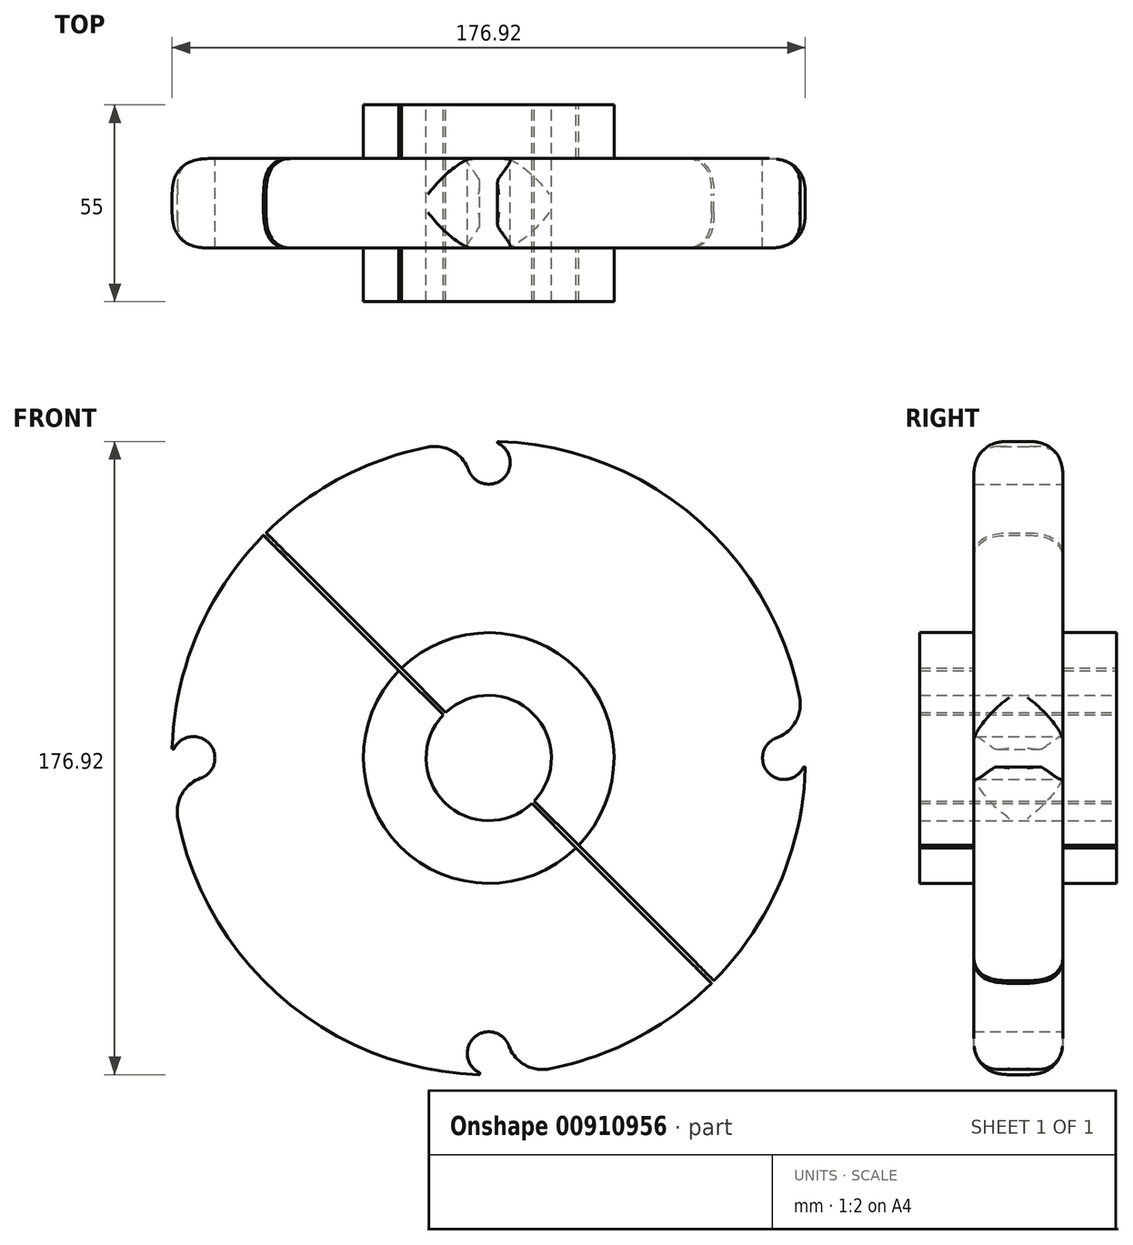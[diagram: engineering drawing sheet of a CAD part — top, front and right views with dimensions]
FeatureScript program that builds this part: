
annotation { "Feature Type Name" : "Feature", "Feature Type Description" : "" }
export const myFeature = defineFeature(function(context is Context, id is Id, definition is map)
    precondition{}
    {
        {
            var Q0;
            Q0=qCreatedBy(makeId("Front.planeOp"),FACE);
            var sketch = newSketch(context, id + "F0", { "sketchPlane" : qUnion([Q0])});
            skArc(sketch, "E0", {"start": v(86.86, 16.96) * mm, "mid": v(57.33, 67.42) * mm, "end": v(2.78, 88.46) * mm});
            skLineSegment(sketch, "E1", {"start": v(-102.93, 0) * mm, "end": v(99.2, 0) * mm, "construction": true});
            skLineSegment(sketch, "E2", {"start": v(0, 101.62) * mm, "end": v(0, -96.77) * mm, "construction": true});
            skCircle(sketch, "E3", {"center": v(0, 0) * mm, "radius": 82.5 * mm, "construction": true});
            skArc(sketch, "E4", {"start": v(80.45, 5.64) * mm, "mid": v(78.03, -4) * mm, "end": v(87.89, -2.64) * mm});
            skArc(sketch, "E5.filletArc", {"start": v(88.46, -2.78) * mm, "mid": v(88.23, -2.48) * mm, "end": v(87.89, -2.64) * mm});
            skArc(sketch, "E6.filletArc", {"start": v(80.45, 5.64) * mm, "mid": v(85.75, 10.12) * mm, "end": v(86.86, 16.96) * mm});
            skArc(sketch, "E7.1.0", {"start": v(-5.64, 80.45) * mm, "mid": v(-10.12, 85.75) * mm, "end": v(-16.96, 86.86) * mm});
            skArc(sketch, "E7.1.1", {"start": v(-5.64, 80.45) * mm, "mid": v(4, 78.03) * mm, "end": v(2.64, 87.89) * mm});
            skArc(sketch, "E7.1.2", {"start": v(2.78, 88.46) * mm, "mid": v(2.48, 88.23) * mm, "end": v(2.64, 87.89) * mm});
            skArc(sketch, "E7.2.0", {"start": v(-80.45, -5.64) * mm, "mid": v(-85.75, -10.12) * mm, "end": v(-86.86, -16.96) * mm});
            skArc(sketch, "E7.2.1", {"start": v(-80.45, -5.64) * mm, "mid": v(-78.03, 4) * mm, "end": v(-87.89, 2.64) * mm});
            skArc(sketch, "E7.2.2", {"start": v(-88.46, 2.78) * mm, "mid": v(-88.23, 2.48) * mm, "end": v(-87.89, 2.64) * mm});
            skArc(sketch, "E7.3.0", {"start": v(5.64, -80.45) * mm, "mid": v(10.12, -85.75) * mm, "end": v(16.96, -86.86) * mm});
            skArc(sketch, "E7.3.1", {"start": v(5.64, -80.45) * mm, "mid": v(-4, -78.03) * mm, "end": v(-2.64, -87.89) * mm});
            skArc(sketch, "E7.3.2", {"start": v(-2.78, -88.46) * mm, "mid": v(-2.48, -88.23) * mm, "end": v(-2.64, -87.89) * mm});
            skArc(sketch, "E8.trimOffspring", {"start": v(-16.96, 86.86) * mm, "mid": v(-67.42, 57.33) * mm, "end": v(-88.46, 2.78) * mm});
            skArc(sketch, "E9.trimOffspring", {"start": v(-86.86, -16.96) * mm, "mid": v(-57.33, -67.42) * mm, "end": v(-2.78, -88.46) * mm});
            skArc(sketch, "E10.trimOffspring", {"start": v(16.96, -86.86) * mm, "mid": v(67.42, -57.33) * mm, "end": v(88.46, -2.78) * mm});
            skCircle(sketch, "E11", {"center": v(0, 0) * mm, "radius": 17.5 * mm});
            skSolve(sketch);
        }
        {
            var Q0;
            Q0 = qSketchRegion(id + "F0", true);
            extrude(context, id + "F1", {"entities" : qUnion([Q0]), "endBound" : BoundingType.SYMMETRIC, "depth" : 25 * mm, "offsetDistance" : 25 * mm});
        }
        {
            var Q0;
            Q0=makeQuery(id+"F1.opExtrude","CAP_EDGE",EDGE,{"disambiguationData":[OSD([sQuery(id+"F0.wireOp",EDGE,"E9.trimOffspring")])],"isStart":false});
            var Q1;
            Q1=makeQuery(id+"F1.opExtrude","CAP_EDGE",EDGE,{"disambiguationData":[OSD([sQuery(id+"F0.wireOp",EDGE,"E8.trimOffspring")])],"isStart":true});
            var Q2;
            Q2=makeQuery(id+"F1.opExtrude","CAP_EDGE",EDGE,{"disambiguationData":[OSD([sQuery(id+"F0.wireOp",EDGE,"E9.trimOffspring")])],"isStart":true});
            var Q3;
            Q3=makeQuery(id+"F1.opExtrude","CAP_EDGE",EDGE,{"disambiguationData":[OSD([sQuery(id+"F0.wireOp",EDGE,"E10.trimOffspring")])],"isStart":false});
            var Q4;
            Q4=makeQuery(id+"F1.opExtrude","CAP_EDGE",EDGE,{"disambiguationData":[OSD([sQuery(id+"F0.wireOp",EDGE,"E10.trimOffspring")])],"isStart":true});
            var Q5;
            Q5=makeQuery(id+"F1.opExtrude","CAP_EDGE",EDGE,{"disambiguationData":[OSD([sQuery(id+"F0.wireOp",EDGE,"E0")])],"isStart":false});
            var Q6;
            Q6=makeQuery(id+"F1.opExtrude","CAP_EDGE",EDGE,{"disambiguationData":[OSD([sQuery(id+"F0.wireOp",EDGE,"E0")])],"isStart":true});
            var Q7;
            Q7=makeQuery(id+"F1.opExtrude","CAP_EDGE",EDGE,{"disambiguationData":[OSD([sQuery(id+"F0.wireOp",EDGE,"E8.trimOffspring")])],"isStart":false});
            fillet(context, id + "F2", {"entities" : qUnion([Q0, Q1, Q2, Q3, Q4, Q5, Q6, Q7]), "radius" : 10 * mm, "rho" : 0.5, "crossSection" : FilletCrossSection.CONIC, "allowEdgeOverflow" : false});
        }
        {
            var Q0;
            Q0=qCreatedBy(makeId("Front.planeOp"),FACE);
            var sketch = newSketch(context, id + "F3", { "sketchPlane" : qUnion([Q0])});
            skCircle(sketch, "E12", {"center": v(0, 0) * mm, "radius": 17.5 * mm});
            skCircle(sketch, "E13", {"center": v(0, 0) * mm, "radius": 35 * mm});
            skSolve(sketch);
        }
        {
            var Q0;
            Q0 = qSketchRegion(id + "F3", true);
            extrude(context, id + "F4", {"entities" : qUnion([Q0]), "operationType" : NewBodyOperationType.ADD, "endBound" : BoundingType.SYMMETRIC, "depth" : 55 * mm, "offsetDistance" : 25 * mm});
        }
        {
            var Q0;
            Q0=qCreatedBy(makeId("Front.planeOp"),FACE);
            var sketch = newSketch(context, id + "F5", { "sketchPlane" : qUnion([Q0])});
            skLineSegment(sketch, "E14", {"start": v(-80.4, 80.4) * mm, "end": v(87.88, -87.88) * mm, "construction": true});
            skLineSegment(sketch, "E15.0", {"start": v(-62.93, 62.22) * mm, "end": v(62.22, -62.93) * mm});
            skLineSegment(sketch, "E16.0", {"start": v(-62.22, 62.93) * mm, "end": v(62.93, -62.22) * mm});
            skArc(sketch, "E17", {"start": v(-62.22, 62.93) * mm, "mid": v(-62.58, 62.58) * mm, "end": v(-62.93, 62.22) * mm});
            skArc(sketch, "E18.trimOffspring", {"start": v(62.22, -62.93) * mm, "mid": v(62.58, -62.58) * mm, "end": v(62.93, -62.22) * mm});
            skSolve(sketch);
        }
        {
            var Q0;
            Q0 = qSketchRegion(id + "F5", true);
            extrude(context, id + "F6", {"entities" : qUnion([Q0]), "operationType" : NewBodyOperationType.REMOVE, "endBound" : BoundingType.SYMMETRIC, "depth" : 60 * mm, "offsetDistance" : 25 * mm});
        }
    });
